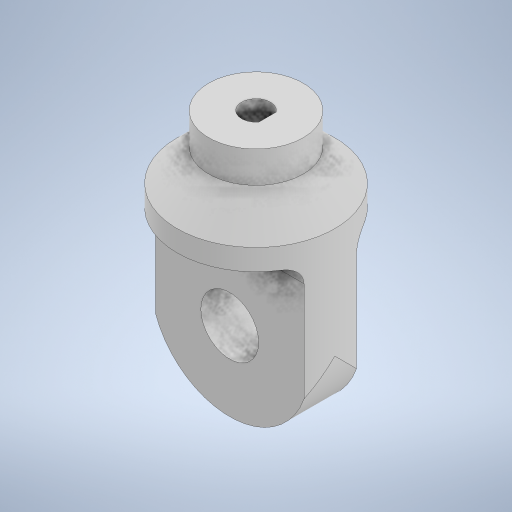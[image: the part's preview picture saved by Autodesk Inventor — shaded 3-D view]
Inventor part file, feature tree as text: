
AUTODESK INVENTOR PART (.ipt)
format: ipt  version: 2023 (Build 270158000, 158)  size: 354,816 bytes
history: native  units: mm
features: sketch x7, extrude x6, projected_geometry x2, other x1, chamfer x1, fillet x1, revolve x1, pattern_circular x1
ambient origin geometry x8: Origin, YZ Plane, XZ Plane, XY Plane, X Axis, Y Axis, Z Axis, Center Point
bodies: Body1 (feature_tree)
feature tree (20):
  other  "솔리드1"
  extrude  "돌출1"  Depth=30.0mm
  extrude  "돌출2"  Depth=10.0mm TaperAngle=0.0deg
  extrude  "돌출3"  Depth=10.0mm
  chamfer  "모따기1"  Distance=32.0mm
  fillet  "모깎기1"  Radius=30.0mm
  revolve  "회전1"
  extrude  "돌출4"  Depth=32.0mm TaperAngle=0.0deg
  pattern_circular  "원형 패턴1"  Angle=45.0deg  [1 undecoded]
  extrude  "돌출5"  Depth=3.0mm
  extrude  "돌출6"  Depth=30.0mm
  sketch  "스케치1"
  sketch  "스케치2"
  projected_geometry  "투영된 루프1"
  sketch  "스케치3"
  sketch  "스케치4"
  sketch  "스케치5"
  sketch  "스케치6"
  projected_geometry  "투영된 루프2"
  sketch  "스케치7"
note: 1 required parameter value undecoded (feature->parameter linkage not recoverable at this tier; creation-order binding heuristic only, values carry confidence <= 0.55)
